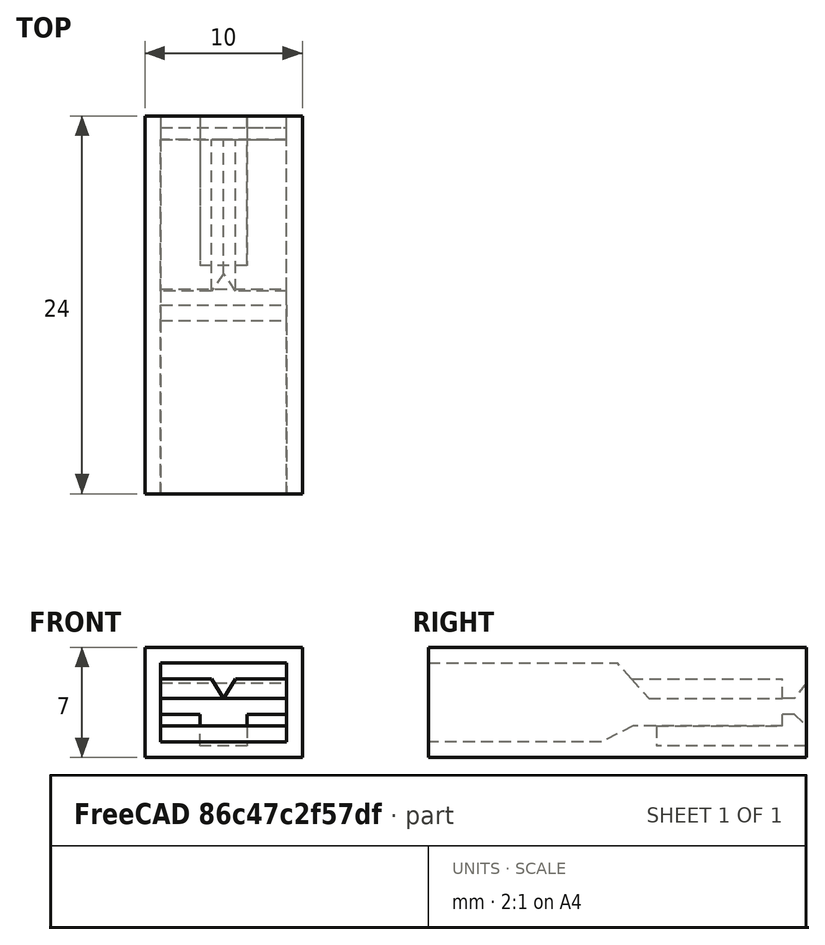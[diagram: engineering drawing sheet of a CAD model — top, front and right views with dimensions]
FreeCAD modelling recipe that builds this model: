
FCSTD DOCUMENT  (FreeCAD 1.0R39109 (Git))
Label: relaybase
License: All rights reserved
LicenseURL: http://en.wikipedia.org/wiki/All_rights_reserved
objects: Sketcher::SketchObject×6, PartDesign::Pad×2, PartDesign::Pocket×2, Mesh::Feature×1, PartDesign::Body×1
note: 25 computed .brp shape members not serialized (recipe doc carries the construction recipe); baked Part::Feature solids carry a one-line shape summary decoded from their .brp

FEATURE [Mesh::Feature] relay_base_holder_5_pin  label="relay-base-holder-5-pin"
FEATURE [Sketcher::SketchObject] Sketch  label="SideProfile"
  ArcFitTolerance = 1e-06
  AttachmentSupport = -> [YZ_Plane]
  FullyConstrained = true
  MakeInternals = false
  MapMode = 5
  Placement = pos=(0,0,0) rot=(0.57735,0.57735,0.57735;2.0944rad)
  sketch-geometry (17):
    g0: LineSegment StartX=0 StartY=0 StartZ=0 EndX=0 EndY=1 EndZ=0
    g1: LineSegment StartX=0 StartY=1 StartZ=0 EndX=11 EndY=1 EndZ=0
    g2: LineSegment StartX=0 StartY=0 StartZ=0 EndX=24 EndY=0 EndZ=0
    g3: LineSegment StartX=11 StartY=1 StartZ=0 EndX=13 EndY=2 EndZ=0
    g4: LineSegment StartX=13 StartY=2 StartZ=0 EndX=22.5 EndY=2 EndZ=0
    g5: LineSegment StartX=22.5 StartY=2 StartZ=0 EndX=22.5 EndY=2.75 EndZ=0
    g6: LineSegment StartX=22.5 StartY=2.75 StartZ=0 EndX=23.25 EndY=2.75 EndZ=0
    g7: LineSegment StartX=23.25 StartY=2.75 StartZ=0 EndX=24 EndY=2 EndZ=0
    g8: LineSegment StartX=24 StartY=2 StartZ=0 EndX=24 EndY=0 EndZ=0
    g9: LineSegment StartX=0 StartY=6 StartZ=0 EndX=12 EndY=6 EndZ=0
    g10: LineSegment StartX=12 StartY=6 StartZ=0 EndX=14 EndY=3.75 EndZ=0
    g11: LineSegment StartX=14 StartY=3.75 StartZ=0 EndX=23.25 EndY=3.75 EndZ=0
    g12: LineSegment StartX=23.25 StartY=3.75 StartZ=0 EndX=24 EndY=4.75 EndZ=0
    g13: LineSegment StartX=24 StartY=4.75 StartZ=0 EndX=24 EndY=7 EndZ=0
    g14: LineSegment StartX=24 StartY=7 StartZ=0 EndX=0 EndY=7 EndZ=0
    g15: LineSegment StartX=0 StartY=7 StartZ=0 EndX=0 EndY=6 EndZ=0
    g16: LineSegment [constr] StartX=23.25 StartY=2.75 StartZ=0 EndX=23.25 EndY=3.75 EndZ=0
  constraints (51):
    c: Coincident(g0,g-1)
    c: PointOnObject(g0,g-2)
    c: Coincident(g1,g0)
    c: Horizontal(g1)
    c: Coincident(g2,g0)
    c: PointOnObject(g2,g-1)
    c: Coincident(g3,g1)
    c: Coincident(g4,g3)
    c: Horizontal(g4)
    c: Coincident(g5,g4)
    c: Vertical(g5)
    c: Coincident(g6,g5)
    c: Horizontal(g6)
    c: Coincident(g7,g6)
    c: Coincident(g8,g7)
    c: Vertical(g8)
    c: Coincident(g2,g8)
    c: DistanceX(g2,g2) = 24
    c: Distance(g0,g0) = 1
    c: Distance(g1,g1) = 11
    c: DistanceX(g0,g3) = 13
    c: DistanceY(g0,g3) = 2
    c: DistanceY(g8,g8) = 2
    c: DistanceY(g2,g6) = 2.75
    c: DistanceX(g6,g7) = 0.75
    c: PointOnObject(g9,g-2)
    c: Horizontal(g9)
    c: Coincident(g10,g9)
    c: Coincident(g11,g10)
    c: Horizontal(g11)
    c: Coincident(g12,g11)
    c: Coincident(g13,g12)
    c: Vertical(g13)
    c: Coincident(g14,g13)
    c: PointOnObject(g14,g-2)
    c: Horizontal(g14)
    c: Coincident(g15,g14)
    c: Coincident(g15,g9)
    c: Distance(g15,g15) = 1
    c: DistanceX(g9,g9) = 12
    c: DistanceX(g9,g10) = 14
    c: Vertical(g11,g6)
    c: DistanceY(g11,g12) = 1
    c: DistanceY(g10,g9) = 2.25
    c: Vertical(g13,g2)
    c: DistanceY(g0,g9) = 5
    c: DistanceX(g4,g4) = 9.5
    c: Coincident(g16,g6)
    c: Coincident(g16,g11)
    c: DistanceY(g16,g16) = 1
    c: DistanceY(g4,g11) = 1.75
FEATURE [PartDesign::Pad] Pad  label="SideProfilePad"
  Direction = (1,0,0)
  Length = 10
  Length2 = 10
  Placement = pos=(0,0,0) rot=(1,1,1;2.0944rad)
  Profile = -> Sketch
  ReferenceAxis = -> Sketch [N_Axis]
  Refine = true
  Suppressed = false
  Type = 0
FEATURE [Sketcher::SketchObject] Sketch001  label="Sides"
  ArcFitTolerance = 1e-06
  AttachmentSupport = -> [XY_Plane]
  ExternalGeometry = -> [Pad]
  FullyConstrained = true
  MakeInternals = false
  MapMode = 5
  sketch-geometry (8):
    g0: LineSegment StartX=-3e-15 StartY=24 StartZ=0 EndX=-3e-15 EndY=0 EndZ=0
    g1: LineSegment StartX=-3e-15 StartY=0 StartZ=0 EndX=1 EndY=0 EndZ=0
    g2: LineSegment StartX=1 StartY=0 StartZ=0 EndX=1 EndY=24 EndZ=0
    g3: LineSegment StartX=1 StartY=24 StartZ=0 EndX=-3e-15 EndY=24 EndZ=0
    g4: LineSegment StartX=10 StartY=24 StartZ=0 EndX=9 EndY=24 EndZ=0
    g5: LineSegment StartX=9 StartY=24 StartZ=0 EndX=9 EndY=0 EndZ=0
    g6: LineSegment StartX=9 StartY=0 StartZ=0 EndX=10 EndY=0 EndZ=0
    g7: LineSegment StartX=10 StartY=0 StartZ=0 EndX=10 EndY=24 EndZ=0
  constraints (22):
    c: Coincident(g0,g1)
    c: Coincident(g1,g2)
    c: Coincident(g2,g3)
    c: Coincident(g3,g0)
    c: Vertical(g0)
    c: Vertical(g2)
    c: Horizontal(g1)
    c: Horizontal(g3)
    c: Coincident(g0,g-3)
    c: PointOnObject(g1,g-1)
    c: Coincident(g4,g5)
    c: Coincident(g5,g6)
    c: Coincident(g6,g7)
    c: Coincident(g7,g4)
    c: Horizontal(g4)
    c: Horizontal(g6)
    c: Vertical(g5)
    c: Vertical(g7)
    c: Coincident(g4,g-4)
    c: PointOnObject(g5,g-1)
    c: Distance(g6,g6) = 1
    c: Distance(g1,g1) = 1
FEATURE [PartDesign::Pad] Pad001  label="SidesPad"
  BaseFeature = -> Pad
  Direction = (0,0,1)
  Length = 6
  Length2 = 10
  Placement = pos=(0,0,0) rot=(1,1,1;2.0944rad)
  Profile = -> Sketch001
  ReferenceAxis = -> Sketch001 [N_Axis]
  Refine = true
  Suppressed = false
  Type = 0
FEATURE [Sketcher::SketchObject] Sketch002  label="Slot"
  ArcFitTolerance = 1e-06
  AttachmentSupport = -> [Pad]
  ExternalGeometry = -> [Pad]
  FullyConstrained = true
  MakeInternals = false
  MapMode = 5
  Placement = pos=(5.3e-15,24,-2.7e-15) rot=(0.57735,0.57735,0.57735;4.18879rad)
  sketch-geometry (6):
    g0: LineSegment StartX=0.75 StartY=6.5 StartZ=0 EndX=0.75 EndY=3.5 EndZ=0
    g1: LineSegment StartX=0.75 StartY=3.5 StartZ=0 EndX=2.75 EndY=3.5 EndZ=0
    g2: LineSegment StartX=2.75 StartY=3.5 StartZ=0 EndX=2.75 EndY=6.5 EndZ=0
    g3: LineSegment StartX=2.75 StartY=6.5 StartZ=0 EndX=0.75 EndY=6.5 EndZ=0
    g4: GeomPoint [constr] X=2.75 Y=5 Z=0
    g5: GeomPoint [constr] X=2.75 Y=5 Z=0
  constraints (13):
    c: Coincident(g0,g1)
    c: Coincident(g1,g2)
    c: Coincident(g2,g3)
    c: Coincident(g3,g0)
    c: Vertical(g0)
    c: Vertical(g2)
    c: Horizontal(g1)
    c: Horizontal(g3)
    c: Distance(g0,g0) = 3
    c: Symmetric(g1,g2,g4)
    c: Symmetric(g-3,g-3,g5)
    c: Coincident(g4,g5)
    c: Distance(g3,g3) = 2
FEATURE [PartDesign::Pocket] Pocket  label="SlotPocket"
  BaseFeature = -> Pad001
  Direction = (0,-1,0)
  Length = 9.5
  Length2 = 5
  Placement = pos=(0,0,0) rot=(1,1,1;2.0944rad)
  Profile = -> Sketch002
  ReferenceAxis = -> Sketch002 [N_Axis]
  Refine = true
  Suppressed = false
  Type = 0
FEATURE [Sketcher::SketchObject] Sketch003  label="PointTrim"
  ArcFitTolerance = 1e-06
  AttachmentSupport = -> [XZ_Plane]
  ExternalGeometry = -> [Pocket]
  FullyConstrained = true
  MakeInternals = false
  MapMode = 5
  Placement = pos=(0,0,0) rot=(1,0,0;1.5708rad)
  sketch-geometry (7):
    g0: LineSegment StartX=1 StartY=5 StartZ=0 EndX=4.23 EndY=5 EndZ=0
    g1: LineSegment StartX=4.23 StartY=5 StartZ=0 EndX=5 EndY=3.75 EndZ=0
    g2: LineSegment StartX=5 StartY=3.75 StartZ=0 EndX=5.77 EndY=5 EndZ=0
    g3: LineSegment StartX=5.77 StartY=5 StartZ=0 EndX=9 EndY=5 EndZ=0
    g4: LineSegment StartX=1 StartY=5 StartZ=0 EndX=1 EndY=3.5 EndZ=0
    g5: LineSegment StartX=1 StartY=3.5 StartZ=0 EndX=9 EndY=3.5 EndZ=0
    g6: LineSegment StartX=9 StartY=3.5 StartZ=0 EndX=9 EndY=5 EndZ=0
  constraints (22):
    c: Horizontal(g0)
    c: Coincident(g1,g0)
    c: Coincident(g2,g1)
    c: Coincident(g3,g2)
    c: Horizontal(g3)
    c: DistanceY(g1,g0) = 1.25
    c: DistanceX(g0,g0) = 3.23
    c: Equal(g3,g0)
    c: Equal(g2,g1)
    c: Coincident(g4,g0)
    c: Vertical(g4)
    c: Coincident(g5,g4)
    c: Horizontal(g5)
    c: Coincident(g6,g5)
    c: Coincident(g6,g3)
    c: Vertical(g6)
    c: DistanceY(g6,g6) = 1.5
    c: Vertical(g0,g-3)
    c: Vertical(g3,g-3)
    c: Horizontal(g0,g2)
    c: DistanceY(g0,g-3) = 1
    c: DistanceY(g-4,g3) = 3
FEATURE [PartDesign::Pocket] Pocket001  label="PointPocket"
  BaseFeature = -> Pocket
  Direction = (0,1,-2e-16)
  Length = 22.5
  Length2 = 5
  Placement = pos=(0,0,0) rot=(1,1,1;2.0944rad)
  Profile = -> Sketch003
  ReferenceAxis = -> Sketch003 [N_Axis]
  Refine = true
  Suppressed = false
  Type = 0
FEATURE [PartDesign::Body] Body  label="PinHousing"
  AllowCompound = true
  Group = -> [Sketch,Pad,Sketch001,Pad001,Sketch002,Pocket,Sketch003,Pocket001]
  Origin = -> Origin
  Tip = -> Pocket001
FEATURE [Sketcher::SketchObject] Sketch004
  ArcFitTolerance = 1e-06
  FullyConstrained = false
  MakeInternals = false
  Placement = pos=(0,0,0) rot=(-0.57735,0.57735,0.57735;4.18879rad)
  sketch-geometry (15):
    g0: LineSegment [constr] StartX=8.99133 StartY=-0.313172 StartZ=0 EndX=15.9913 EndY=-0.313172 EndZ=0
    g1: LineSegment [constr] StartX=16.5236 StartY=0 StartZ=0 EndX=16.5236 EndY=11 EndZ=0
    g2: LineSegment [constr] StartX=8.44964 StartY=12.0789 StartZ=0 EndX=8.44964 EndY=0.078882 EndZ=0
    g3: LineSegment [constr] StartX=11.9786 StartY=13.9896 StartZ=0 EndX=11.9786 EndY=23.2396 EndZ=0
    g4: LineSegment [constr] StartX=13.6744 StartY=12.9951 StartZ=0 EndX=13.6744 EndY=22.4951 EndZ=0
    g5: LineSegment [constr] StartX=11.337 StartY=24.7513 StartZ=0 EndX=13.837 EndY=24.7513 EndZ=0
    g6: LineSegment [constr] StartX=12.085 StartY=26.2116 StartZ=0 EndX=13.085 EndY=26.2116 EndZ=0
    g7: LineSegment [constr] StartX=10.4776 StartY=12.6009 StartZ=0 EndX=13.9776 EndY=12.6009 EndZ=0
    g8: LineSegment [constr] StartX=10.4934 StartY=22.4929 StartZ=0 EndX=10.4934 EndY=12.9929 EndZ=0
    g9: LineSegment [constr] StartX=12.0792 StartY=22.4993 StartZ=0 EndX=12.0631 EndY=23.2493 EndZ=0
    g10: LineSegment [constr] StartX=14.0023 StartY=12.8576 StartZ=0 EndX=16.0023 EndY=12.8576 EndZ=0
    g11: LineSegment [constr] StartX=16.5236 StartY=0 StartZ=0 EndX=16.5236 EndY=13 EndZ=0
    g12: LineSegment [constr] StartX=11.7272 StartY=14 StartZ=0 EndX=11.7272 EndY=0 EndZ=0
    g13: LineSegment [constr] StartX=11.9786 StartY=15.4723 StartZ=0 EndX=8.97861 EndY=15.4723 EndZ=0
    g14: LineSegment [constr] StartX=14.008 StartY=22.0652 StartZ=0 EndX=13.008 EndY=22.0652 EndZ=0
  constraints (33):
    c: Horizontal(g0)
    c: PointOnObject(g1,g-1)
    c: Vertical(g1)
    c: Vertical(g2)
    c: Vertical(g3)
    c: Vertical(g4)
    c: Horizontal(g5)
    c: DistanceX(g0,g0) = 7
    c: DistanceY(g2,g2) = 12
    c: DistanceY(g1,g1) = 11
    c: DistanceY(g4,g4) = 9.5
    c: DistanceY(g3,g3) = 9.25
    c: Distance(g5,g5) = 2.5
    c: Horizontal(g6)
    c: Distance(g6,g6) = 1
    c: Horizontal(g7)
    c: Vertical(g8)
    c: DistanceY(g8,g8) = 9.5
    c: DistanceX(g7,g7) = 3.5
    c: DistanceY(g9,g9) = 0.75
    c: Horizontal(g10)
    c: DistanceX(g10,g10) = 2
    c: Coincident(g11,g1)
    c: Vertical(g11)
    c: DistanceY(g11,g11) = 13
    c: PointOnObject(g12,g-1)
    c: Vertical(g12)
    c: DistanceY(g12,g12) = 14
    c: PointOnObject(g13,g3)
    c: Horizontal(g13)
    c: Distance(g13,g13) = 3
    c: Horizontal(g14)
    c: DistanceX(g14,g14) = 1
FEATURE [Sketcher::SketchObject] Sketch005
  ArcFitTolerance = 1e-06
  FullyConstrained = false
  MakeInternals = false
  sketch-geometry (1):
    g0: LineSegment [constr] StartX=-2.97869 StartY=-21.3928 StartZ=0 EndX=-2.97869 EndY=-23.3928 EndZ=0
  constraints (2):
    c: Vertical(g0)
    c: DistanceY(g0,g0) = 2
